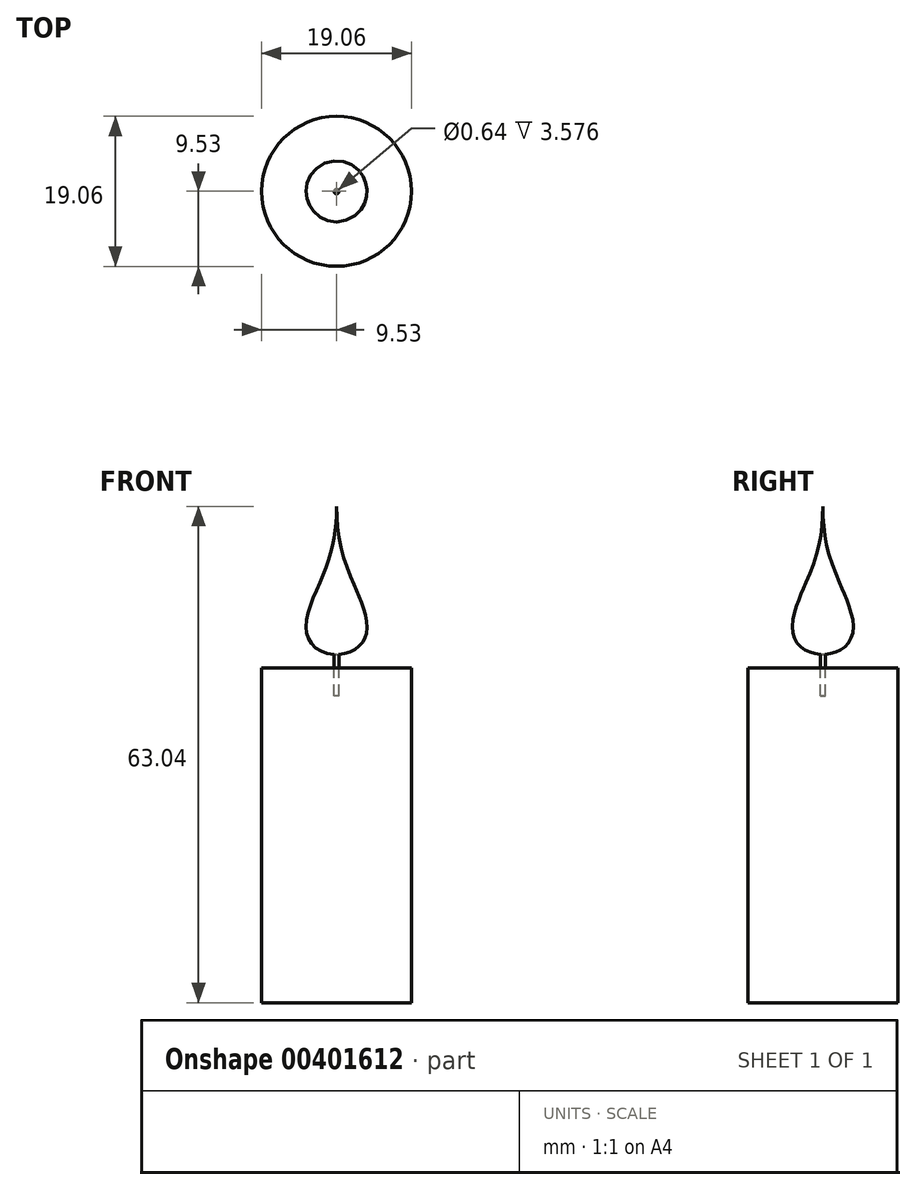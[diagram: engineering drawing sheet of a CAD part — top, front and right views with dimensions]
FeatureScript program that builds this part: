
annotation { "Feature Type Name" : "Feature", "Feature Type Description" : "" }
export const myFeature = defineFeature(function(context is Context, id is Id, definition is map)
    precondition{}
    {
        {
            var Q0;
            Q0=qCreatedBy(makeId("Front.planeOp"),FACE);
            var sketch = newSketch(context, id + "F0", { "sketchPlane" : qUnion([Q0])});
            skFitSpline(sketch, "E0", {"points": [v(0, 0) * mm, v(-3.83, 2.8) * mm, v(-1.5, 10.65) * mm, v(0, 19.05) * mm], "startDerivative": vector(-22.29, 0.15) * mm, "endDerivative": vector(-0.1, 26.34) * mm});
            skLineSegment(sketch, "E1", {"start": v(0, 19.05) * mm, "end": v(0, 0) * mm});
            skLineSegment(sketch, "E2.bottom", {"start": v(-0.32, 1.52) * mm, "end": v(0, 1.52) * mm});
            skLineSegment(sketch, "E2.top", {"start": v(-0.32, -5.28) * mm, "end": v(0, -5.28) * mm});
            skLineSegment(sketch, "E2.left", {"start": v(-0.32, 1.52) * mm, "end": v(-0.32, -5.28) * mm});
            skLineSegment(sketch, "E2.right", {"start": v(0, 1.52) * mm, "end": v(0, -5.28) * mm});
            skLineSegment(sketch, "E3.bottom", {"start": v(-9.53, -1.7) * mm, "end": v(0, -1.7) * mm});
            skLineSegment(sketch, "E3.top", {"start": v(-9.52, -44.23) * mm, "end": v(0, -44.23) * mm});
            skLineSegment(sketch, "E3.left", {"start": v(-9.53, -1.7) * mm, "end": v(-9.52, -44.23) * mm});
            skLineSegment(sketch, "E3.right", {"start": v(0, -1.7) * mm, "end": v(0, -44.23) * mm});
            skSolve(sketch);
        }
        {
            var Q0;
            Q0=makeQuery(id+"F0.imprint","IMPRINT",FACE,{"disambiguationData":[TD([[makeQuery(id+"F0.imprint","IMPRINT",EDGE,{"derivedFrom":sQuery(id+"F0.wireOp",EDGE,"E0")}),-1.0]])]});
            var Q1;
            Q1=sQuery(id+"F0.wireOp",EDGE,"E1");
            revolve(context, id + "F1", {"entities" : qUnion([Q0]), "axis" : qUnion([Q1]), "revolveType" : RevolveType.FULL});
        }
        {
            var Q0;
            {var subQ0=sQuery(id+"F0.wireOp",EDGE,"E2.right");var subQ1=sQuery(id+"F0.wireOp",EDGE,"E0");var subQ2=makeQuery(id+"F0.imprint","INTERSECT",VERTEX,{"derivedFrom":[subQ1,subQ0]});Q0=makeQuery(id+"F0.imprint","IMPRINT",FACE,{"disambiguationData":[TD([[makeQuery(id+"F0.imprint","IMPRINT",EDGE,{"disambiguationData":[TD([[subQ2,-1.0]])],"derivedFrom":subQ1}),1.0]])]});}
            var Q1;
            Q1=sQuery(id+"F0.wireOp",EDGE,"E2.right");
            revolve(context, id + "F2", {"entities" : qUnion([Q0]), "axis" : qUnion([Q1]), "revolveType" : RevolveType.FULL});
        }
        {
            var Q0;
            {var subQ5=sQuery(id+"F0.wireOp",EDGE,"E2.top");Q0=makeQuery(id+"F0.imprint","IMPRINT",FACE,{"disambiguationData":[TD([[makeQuery(id+"F0.imprint","IMPRINT",EDGE,{"derivedFrom":subQ5}),-1.0]])]});}
            var Q1;
            Q1=sQuery(id+"F0.wireOp",EDGE,"E3.right");
            revolve(context, id + "F3", {"entities" : qUnion([Q0]), "axis" : qUnion([Q1]), "revolveType" : RevolveType.FULL});
        }
    });
